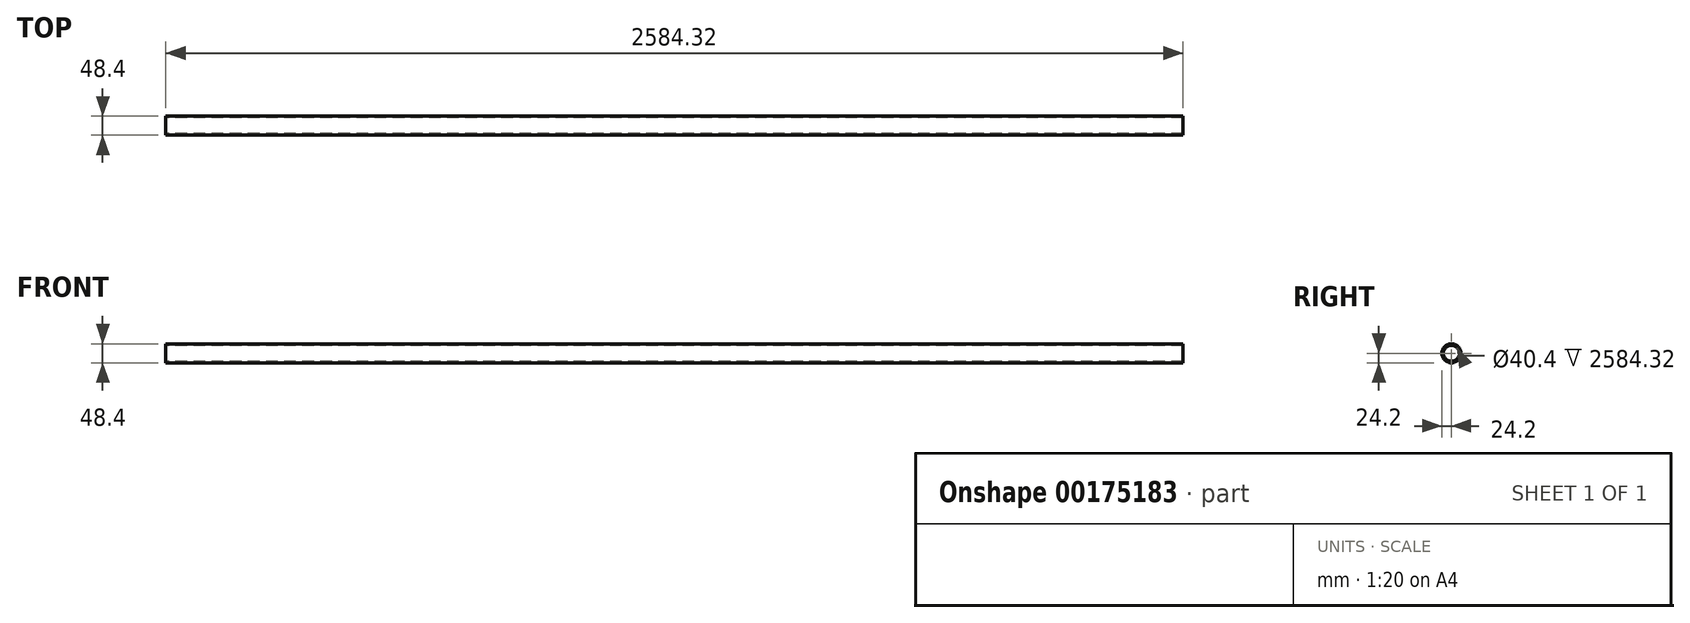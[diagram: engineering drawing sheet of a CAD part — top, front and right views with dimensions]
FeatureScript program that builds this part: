
annotation { "Feature Type Name" : "Feature", "Feature Type Description" : "" }
export const myFeature = defineFeature(function(context is Context, id is Id, definition is map)
    precondition{}
    {
        {
            var Q0;
            Q0=qCreatedBy(makeId("Right.planeOp"),FACE);
            var sketch = newSketch(context, id + "F0", { "sketchPlane" : qUnion([Q0])});
            skCircle(sketch, "E0", {"center": v(0, 0) * mm, "radius": 24.2 * mm});
            skSolve(sketch);
        }
        {
            var Q0;
            Q0=qSketchRegion(id+"F0",true);
            extrude(context, id + "F1", {"entities" : qUnion([Q0]), "depth" : 2584.32 * mm});
        }
        {
            var Q0;
            Q0=makeQuery(id+"F1.opExtrude","CAP_FACE",FACE,{"disambiguationData":[OSD([sQuery(id+"F0.wireOp",EDGE,"E0")])],"isStart":false});
            var Q1;
            Q1=makeQuery(id+"F1.opExtrude","CAP_FACE",FACE,{"disambiguationData":[OSD([sQuery(id+"F0.wireOp",EDGE,"E0")])],"isStart":true});
            shell(context, id + "F2", {"entities" : qUnion([Q0, Q1]), "thickness" : 4 * mm});
        }
    });
